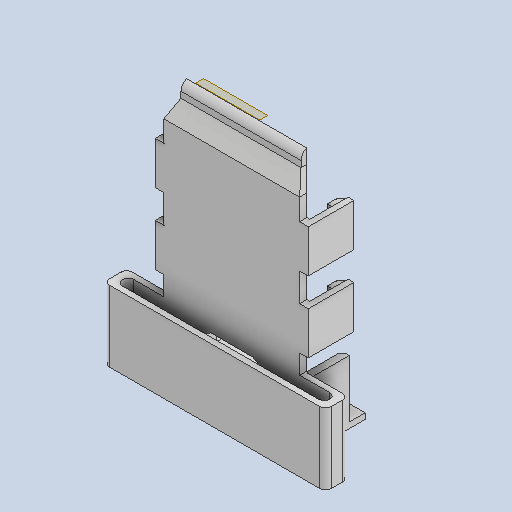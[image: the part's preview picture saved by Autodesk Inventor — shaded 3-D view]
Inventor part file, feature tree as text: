
AUTODESK INVENTOR PART (.ipt)
format: ipt  version: 2023.4 (Build 274418000, 418)  size: 380,416 bytes
history: native  units: mm
features: reference x31, extrude x9, other x8, chamfer x4, plane x3, fillet x3, loft x2, sketch x2
ambient origin geometry x8: Origin, YZ Plane, XZ Plane, XY Plane, X Axis, Y Axis, Z Axis, Center Point
bodies: Solid1 (feature_tree)
feature tree (62):
  extrude  "base_plane"  Depth=0.608mm
  extrude  "tabs"  Depth=2.7mm TaperAngle=0.0deg
  plane  "Work Plane1"
  extrude  "top"  Depth=0.5mm
  extrude  "sides"  Depth=2.7mm TaperAngle=0.0deg
  extrude  "tab_knobs_1"  Depth=0.5mm
  extrude  "tab_knobs_2"  Depth=0.5mm
  chamfer  "Chamfer1"  Distance=2.983mm
  chamfer  "Chamfer2"  Distance=0.1mm
  plane  "Work Plane2"
  plane  "Work Plane3"
  loft  "Loft1"
  loft  "Loft2"
  fillet  "Fillet1"  Radius=0.1mm
  extrude  "Extrusion12"  Depth=0.5mm
  extrude  "Extrusion13"  Depth=0.5mm
  extrude  "Extrusion14"  Depth=0.2mm TaperAngle=45.0deg
  fillet  "Fillet2"  Radius=0.3mm
  fillet  "Fillet3"  Radius=0.2mm
  chamfer  "Chamfer3"  Distance=0.2mm
  chamfer  "Chamfer4"  Distance=0.2mm
  reference  "Reference1"
  reference  "Reference4"
  reference  "Reference5"
  reference  "Reference6"
  reference  "Reference7"
  reference  "Reference8"
  reference  "Reference9"
  reference  "Reference10"
  reference  "Reference11"
  reference  "Reference12"
  reference  "Reference13"
  reference  "Reference14"
  reference  "Reference15"
  reference  "Reference16"
  reference  "Reference17"
  reference  "Reference18"
  reference  "Reference19"
  reference  "Reference20"
  reference  "Reference21"
  reference  "Reference22"
  reference  "Reference23"
  reference  "Reference24"
  reference  "Reference25"
  reference  "Reference26"
  reference  "Reference27"
  reference  "Reference30"
  reference  "Reference31"
  reference  "Reference32"
  reference  "Reference33"
  reference  "Reference34"
  reference  "Reference35"
  other  "Edges1"
  sketch  "Sketch14"  dims[d0=0.508mm d1=0.608mm]
  sketch  "Sketch16"  dims[d2=0.508mm d3=0.0mm d4=2.7mm d5=0.0mm d6=0.1mm d7=2.7mm d8=0.0mm d9=0.05mm d10=0.05mm d11=2.983mm d12=0.0mm d13=0.1mm d14=0.1mm d17=0.1mm d20=0.1mm d21=0.5mm d22=-1.745329mm d23=0.5mm d24=-1.745329mm d35=0.2mm d36=2.0mm d37=45.0deg d38=0.3mm d39=2.0mm d40=45.0deg d41=0.2mm d42=0.2mm d43=0.2mm d44=1.0mm d45=1.0mm d46=0.4mm d47=0.0mm d48=90.0deg d49=0.0mm d50=90.0deg d53=0.0mm d54=90.0deg d55=0.6mm d68=0.4mm d70=0.4mm d72=0.5mm d73=0.5mm d76=5.0mm d77=0.0mm d78=0.3mm d79=0.0mm d80=0.3mm d81=0.3mm d82=0.0mm d83=0.0mm d84=90.0deg d85=0.2mm d87=0.8mm d89=14.6mm d90=0.4mm d91=1.5mm d92=2.5mm d93=45.0deg d94=2.5mm d95=1.5mm d96=45.0deg d86=0.5mm d88=0.5mm]
  other  "Edges4"
  parser-record x2  (decoder bookkeeping rows leaked as tree rows — omitted from the tree; the rows remain in map.json)
  other  "np1_full_assembly.iam"
  other  "np1_main_chassis:1"
  other  "full_assembly.iam"
  other  "probe_holder:1"
note: 2 file-system paths scrubbed to <path> (originals preserved in map.json)
